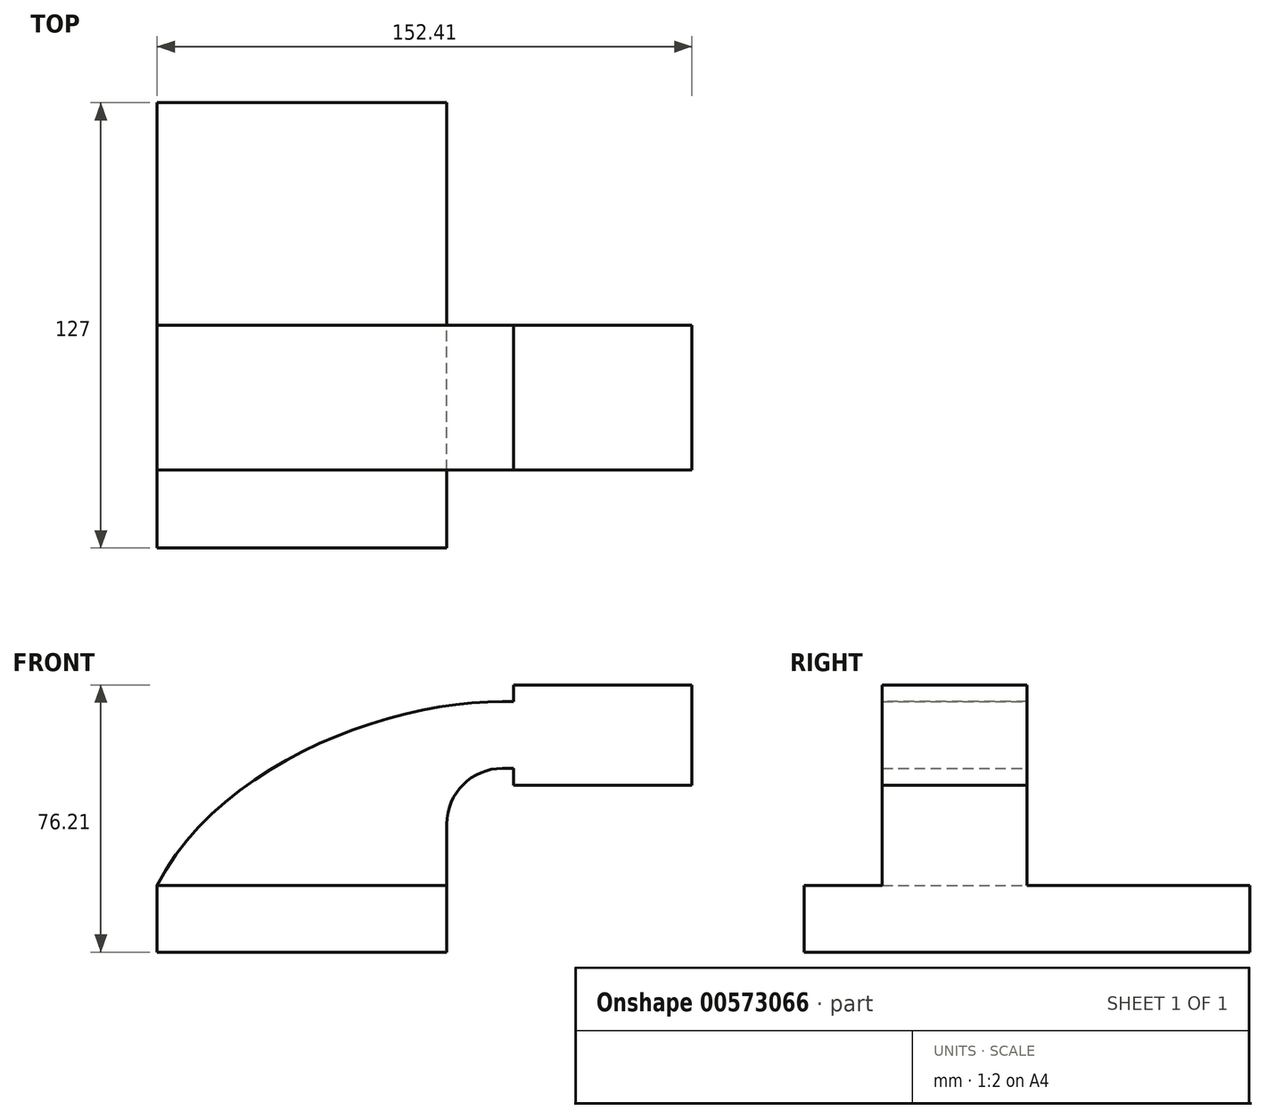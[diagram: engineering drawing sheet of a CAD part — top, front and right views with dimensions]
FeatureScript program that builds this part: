
annotation { "Feature Type Name" : "Feature", "Feature Type Description" : "" }
export const myFeature = defineFeature(function(context is Context, id is Id, definition is map)
    precondition{}
    {
        {
            var Q0;
            Q0=qCreatedBy(makeId("Front.planeOp"),FACE);
            var sketch = newSketch(context, id + "F0", { "sketchPlane" : qUnion([Q0])});
            skLineSegment(sketch, "E0.bottom", {"start": v(41.28, -9.52) * mm, "end": v(-41.27, -9.53) * mm});
            skLineSegment(sketch, "E0.top", {"start": v(41.27, 9.53) * mm, "end": v(-41.28, 9.53) * mm});
            skLineSegment(sketch, "E0.left", {"start": v(41.28, -9.52) * mm, "end": v(41.28, 9.53) * mm});
            skLineSegment(sketch, "E0.right", {"start": v(-41.27, -9.53) * mm, "end": v(-41.28, 9.53) * mm});
            skPoint(sketch, "E0.middle", {"position": v(0, 0) * mm});
            skLineSegment(sketch, "E1.bottom", {"start": v(111.12, 38.1) * mm, "end": v(60.32, 38.1) * mm});
            skLineSegment(sketch, "E1.top", {"start": v(111.12, 66.68) * mm, "end": v(60.32, 66.67) * mm});
            skLineSegment(sketch, "E1.left", {"start": v(111.12, 38.1) * mm, "end": v(111.12, 66.68) * mm});
            skLineSegment(sketch, "E1.right", {"start": v(60.32, 38.1) * mm, "end": v(60.32, 66.67) * mm});
            skPoint(sketch, "E1.middle", {"position": v(85.72, 52.39) * mm});
            skLineSegment(sketch, "E2", {"start": v(41.27, 9.53) * mm, "end": v(41.27, 27) * mm});
            skArc(sketch, "E3", {"start": v(41.27, 27) * mm, "mid": v(45.92, 38.23) * mm, "end": v(57.15, 42.88) * mm});
            skLineSegment(sketch, "E4", {"start": v(57.15, 42.88) * mm, "end": v(85.72, 42.88) * mm});
            skLineSegment(sketch, "E5.0", {"start": v(57.15, 61.93) * mm, "end": v(85.72, 61.93) * mm});
            skArc(sketch, "E5.1", {"start": v(22.23, 27) * mm, "mid": v(32.45, 51.7) * mm, "end": v(57.15, 61.93) * mm});
            skLineSegment(sketch, "E5.2", {"start": v(22.22, 9.53) * mm, "end": v(22.22, 27) * mm});
            skLineSegment(sketch, "E6", {"start": v(85.72, 38.1) * mm, "end": v(85.72, 66.68) * mm});
            skFitSpline(sketch, "E7", {"points": [v(-41.28, 9.52) * mm, v(57.15, 61.93) * mm], "startDerivative": vector(53.44, 104.54) * mm, "endDerivative": vector(96.47, -0.39) * mm});
            skSolve(sketch);
        }
        {
            var Q0;
            Q0=makeQuery(id+"F0.imprint","IMPRINT",FACE,{"disambiguationData":[TD([[makeQuery(id+"F0.imprint","IMPRINT",EDGE,{"derivedFrom":sQuery(id+"F0.wireOp",EDGE,"E0.bottom")}),-1.0]])]});
            extrude(context, id + "F1", {"entities" : qUnion([Q0]), "endBound" : BoundingType.SYMMETRIC, "depth" : 127 * mm, "offsetDistance" : 25.4 * mm});
        }
        {
            var Q0;
            Q0 = qSketchRegion(id + "F0", true);
            extrude(context, id + "F2", {"entities" : qUnion([Q0]), "operationType" : NewBodyOperationType.ADD, "depth" : 25.4 * mm, "offsetDistance" : 25.4 * mm});
        }
        {
            var Q0;
            Q0 = qSketchRegion(id + "F0", true);
            var Q1;
            Q1=makeQuery(id+"F2.opExtrude","CAP_FACE",FACE,{"disambiguationData":[OSD([sQuery(id+"F0.wireOp",EDGE,"E0.bottom"),sQuery(id+"F0.wireOp",EDGE,"E0.left"),sQuery(id+"F0.wireOp",EDGE,"E0.right"),sQuery(id+"F0.wireOp",EDGE,"E1.bottom"),sQuery(id+"F0.wireOp",EDGE,"E1.top"),sQuery(id+"F0.wireOp",EDGE,"E1.left"),sQuery(id+"F0.wireOp",EDGE,"E1.right"),sQuery(id+"F0.wireOp",EDGE,"E2"),sQuery(id+"F0.wireOp",EDGE,"E3"),sQuery(id+"F0.wireOp",EDGE,"E4"),sQuery(id+"F0.wireOp",EDGE,"E5.0"),sQuery(id+"F0.wireOp",EDGE,"E7")])],"isStart":false});
            extrude(context, id + "F3", {"entities" : qUnion([Q0, Q1]), "operationType" : NewBodyOperationType.ADD, "depth" : 15.88 * mm, "offsetDistance" : 25.4 * mm});
        }
    });
